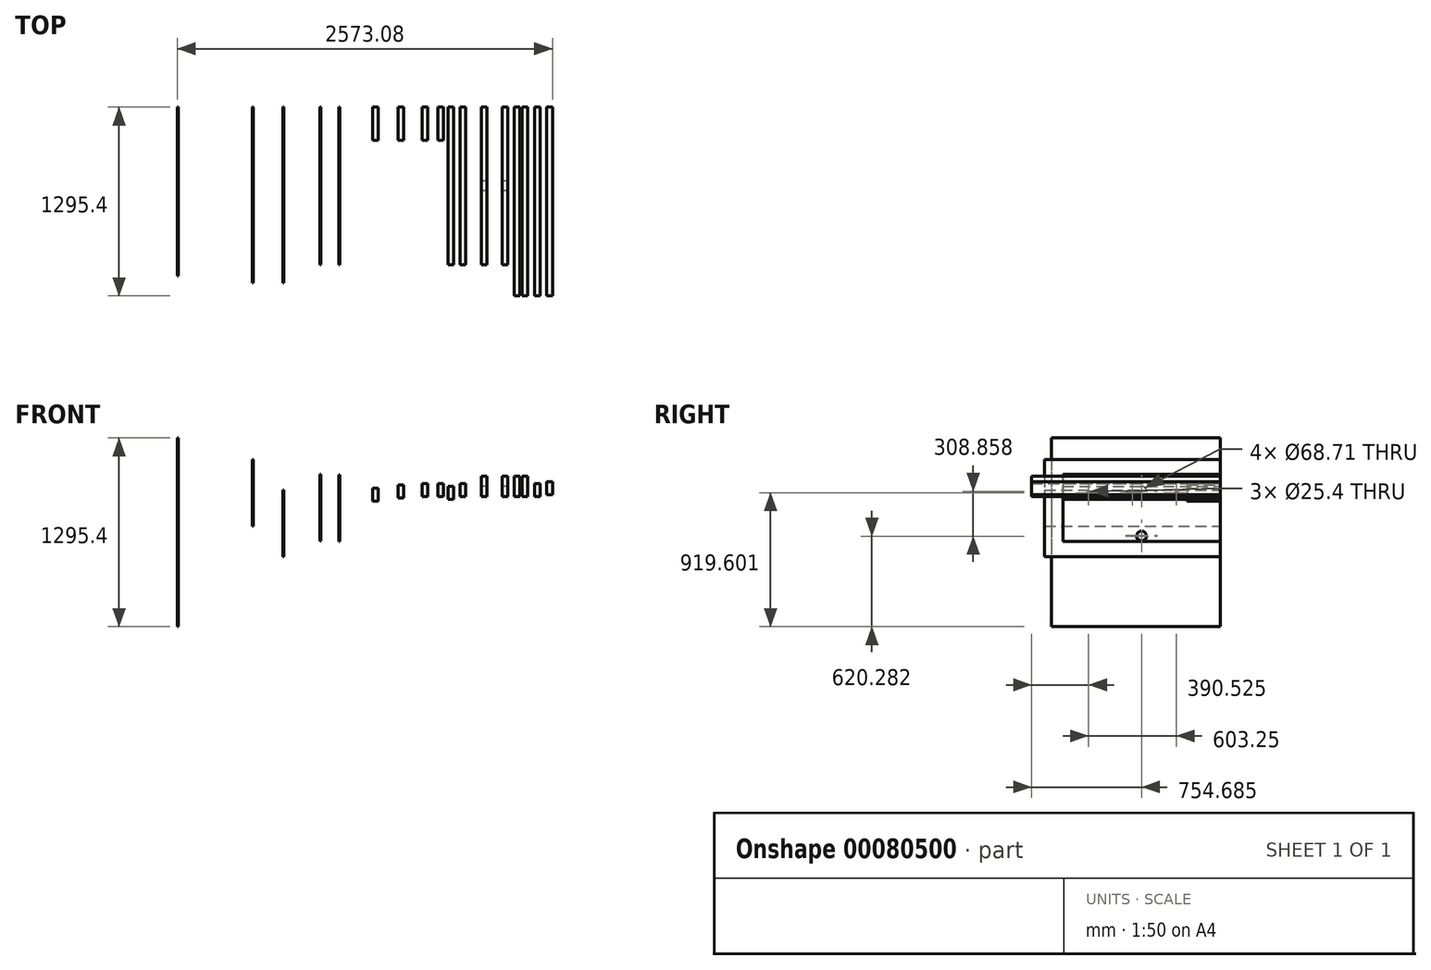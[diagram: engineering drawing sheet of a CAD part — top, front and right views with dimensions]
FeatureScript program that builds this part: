
annotation { "Feature Type Name" : "Feature", "Feature Type Description" : "" }
export const myFeature = defineFeature(function(context is Context, id is Id, definition is map)
    precondition{}
    {
        {
            var Q0;
            Q0=qCreatedBy(makeId("Front.planeOp"),FACE);
            var sketch = newSketch(context, id + "F0", { "sketchPlane" : qUnion([Q0])});
            skLineSegment(sketch, "E0.bottom", {"start": v(0, 0) * mm, "end": v(38.1, 0) * mm});
            skLineSegment(sketch, "E0.top", {"start": v(0, 139.7) * mm, "end": v(38.1, 139.7) * mm});
            skLineSegment(sketch, "E0.left", {"start": v(0, 0) * mm, "end": v(0, 139.7) * mm});
            skLineSegment(sketch, "E0.right", {"start": v(38.1, 0) * mm, "end": v(38.1, 139.7) * mm});
            skSolve(sketch);
        }
        {
            var Q0;
            Q0 = qSketchRegion(id + "F0", true);
            extrude(context, id + "F1", {"entities" : qUnion([Q0]), "depth" : 1295.4 * mm});
        }
        {
            var Q0;
            Q0=qCreatedBy(makeId("Front.planeOp"),FACE);
            var sketch = newSketch(context, id + "F2", { "sketchPlane" : qUnion([Q0])});
            skLineSegment(sketch, "E1.bottom", {"start": v(-55.83, 0) * mm, "end": v(-17.73, 0) * mm});
            skLineSegment(sketch, "E1.top", {"start": v(-55.83, 139.7) * mm, "end": v(-17.73, 139.7) * mm});
            skLineSegment(sketch, "E1.left", {"start": v(-55.83, 0) * mm, "end": v(-55.83, 139.7) * mm});
            skLineSegment(sketch, "E1.right", {"start": v(-17.73, 0) * mm, "end": v(-17.73, 139.7) * mm});
            skSolve(sketch);
        }
        {
            var Q0;
            Q0 = qSketchRegion(id + "F2", true);
            extrude(context, id + "F3", {"entities" : qUnion([Q0]), "depth" : 1295.4 * mm});
        }
        {
            var Q0;
            Q0=qCreatedBy(makeId("Front.planeOp"),FACE);
            var sketch = newSketch(context, id + "F4", { "sketchPlane" : qUnion([Q0])});
            skLineSegment(sketch, "E2.bottom", {"start": v(-138.64, 0) * mm, "end": v(-100.54, 0) * mm});
            skLineSegment(sketch, "E2.top", {"start": v(-138.64, 139.7) * mm, "end": v(-100.54, 139.7) * mm});
            skLineSegment(sketch, "E2.left", {"start": v(-138.64, 0) * mm, "end": v(-138.64, 139.7) * mm});
            skLineSegment(sketch, "E2.right", {"start": v(-100.54, 0) * mm, "end": v(-100.54, 139.7) * mm});
            skSolve(sketch);
        }
        {
            var Q0;
            Q0 = qSketchRegion(id + "F4", true);
            extrude(context, id + "F5", {"entities" : qUnion([Q0]), "depth" : 1081.43 * mm});
        }
        {
            var Q0;
            Q0=qCreatedBy(makeId("Front.planeOp"),FACE);
            var sketch = newSketch(context, id + "F6", { "sketchPlane" : qUnion([Q0])});
            skLineSegment(sketch, "E3.bottom", {"start": v(-281.16, 0) * mm, "end": v(-243.06, 0) * mm});
            skLineSegment(sketch, "E3.top", {"start": v(-281.16, 139.7) * mm, "end": v(-243.06, 139.7) * mm});
            skLineSegment(sketch, "E3.left", {"start": v(-281.16, 0) * mm, "end": v(-281.16, 139.7) * mm});
            skLineSegment(sketch, "E3.right", {"start": v(-243.06, 0) * mm, "end": v(-243.06, 139.7) * mm});
            skSolve(sketch);
        }
        {
            var Q0;
            Q0 = qSketchRegion(id + "F6", true);
            extrude(context, id + "F7", {"entities" : qUnion([Q0]), "depth" : 1081.43 * mm});
        }
        {
            var Q0;
            Q0=qCreatedBy(makeId("Front.planeOp"),FACE);
            var sketch = newSketch(context, id + "F8", { "sketchPlane" : qUnion([Q0])});
            skLineSegment(sketch, "E4.bottom", {"start": v(-507.98, 70.18) * mm, "end": v(-469.88, 70.18) * mm});
            skLineSegment(sketch, "E4.top", {"start": v(-507.98, -18.72) * mm, "end": v(-469.88, -18.72) * mm});
            skLineSegment(sketch, "E4.left", {"start": v(-507.98, 70.18) * mm, "end": v(-507.98, -18.72) * mm});
            skLineSegment(sketch, "E4.right", {"start": v(-469.88, 70.18) * mm, "end": v(-469.88, -18.72) * mm});
            skSolve(sketch);
        }
        {
            var Q0;
            Q0 = qSketchRegion(id + "F8", true);
            extrude(context, id + "F9", {"entities" : qUnion([Q0]), "depth" : 1081.43 * mm});
        }
        {
            var Q0;
            Q0=qCreatedBy(makeId("Front.planeOp"),FACE);
            var sketch = newSketch(context, id + "F10", { "sketchPlane" : qUnion([Q0])});
            skLineSegment(sketch, "E5.bottom", {"start": v(-426.13, 1.44) * mm, "end": v(-388.03, 1.44) * mm});
            skLineSegment(sketch, "E5.top", {"start": v(-426.13, 90.34) * mm, "end": v(-388.03, 90.34) * mm});
            skLineSegment(sketch, "E5.left", {"start": v(-426.13, 1.44) * mm, "end": v(-426.13, 90.34) * mm});
            skLineSegment(sketch, "E5.right", {"start": v(-388.03, 1.44) * mm, "end": v(-388.03, 90.34) * mm});
            skSolve(sketch);
        }
        {
            var Q0;
            Q0 = qSketchRegion(id + "F10", true);
            extrude(context, id + "F11", {"entities" : qUnion([Q0]), "depth" : 1081.43 * mm});
        }
        {
            var Q0;
            Q0=qCreatedBy(makeId("Front.planeOp"),FACE);
            var sketch = newSketch(context, id + "F12", { "sketchPlane" : qUnion([Q0])});
            skLineSegment(sketch, "E6.bottom", {"start": v(86.38, 88.9) * mm, "end": v(124.48, 88.9) * mm});
            skLineSegment(sketch, "E6.top", {"start": v(86.38, 0) * mm, "end": v(124.48, 0) * mm});
            skLineSegment(sketch, "E6.left", {"start": v(86.38, 88.9) * mm, "end": v(86.38, 0) * mm});
            skLineSegment(sketch, "E6.right", {"start": v(124.48, 88.9) * mm, "end": v(124.48, 0) * mm});
            skSolve(sketch);
        }
        {
            var Q0;
            Q0 = qSketchRegion(id + "F12", true);
            extrude(context, id + "F13", {"entities" : qUnion([Q0]), "depth" : 1295.4 * mm});
        }
        {
            var Q0;
            Q0=qCreatedBy(makeId("Front.planeOp"),FACE);
            var sketch = newSketch(context, id + "F14", { "sketchPlane" : qUnion([Q0])});
            skLineSegment(sketch, "E7.bottom", {"start": v(169.11, 101.24) * mm, "end": v(207.21, 101.24) * mm});
            skLineSegment(sketch, "E7.top", {"start": v(169.11, 12.34) * mm, "end": v(207.21, 12.34) * mm});
            skLineSegment(sketch, "E7.left", {"start": v(169.11, 101.24) * mm, "end": v(169.11, 12.34) * mm});
            skLineSegment(sketch, "E7.right", {"start": v(207.21, 101.24) * mm, "end": v(207.21, 12.34) * mm});
            skSolve(sketch);
        }
        {
            var Q0;
            Q0 = qSketchRegion(id + "F14", true);
            extrude(context, id + "F15", {"entities" : qUnion([Q0]), "depth" : 1295.4 * mm});
        }
        {
            var Q0;
            Q0=qCreatedBy(makeId("Front.planeOp"),FACE);
            var sketch = newSketch(context, id + "F16", { "sketchPlane" : qUnion([Q0])});
            skLineSegment(sketch, "E8.bottom", {"start": v(-687.17, 0) * mm, "end": v(-649.07, 0) * mm});
            skLineSegment(sketch, "E8.top", {"start": v(-687.17, 88.9) * mm, "end": v(-649.07, 88.9) * mm});
            skLineSegment(sketch, "E8.left", {"start": v(-687.17, 0) * mm, "end": v(-687.17, 88.9) * mm});
            skLineSegment(sketch, "E8.right", {"start": v(-649.07, 0) * mm, "end": v(-649.07, 88.9) * mm});
            skSolve(sketch);
        }
        {
            var Q0;
            Q0 = qSketchRegion(id + "F16", true);
            extrude(context, id + "F17", {"entities" : qUnion([Q0]), "depth" : 228.6 * mm});
        }
        {
            var Q0;
            Q0=qCreatedBy(makeId("Front.planeOp"),FACE);
            var sketch = newSketch(context, id + "F18", { "sketchPlane" : qUnion([Q0])});
            skLineSegment(sketch, "E9.bottom", {"start": v(-579.7, 88.9) * mm, "end": v(-541.6, 88.9) * mm});
            skLineSegment(sketch, "E9.top", {"start": v(-579.7, 0) * mm, "end": v(-541.6, 0) * mm});
            skLineSegment(sketch, "E9.left", {"start": v(-579.7, 88.9) * mm, "end": v(-579.7, 0) * mm});
            skLineSegment(sketch, "E9.right", {"start": v(-541.6, 88.9) * mm, "end": v(-541.6, 0) * mm});
            skSolve(sketch);
        }
        {
            var Q0;
            Q0 = qSketchRegion(id + "F18", true);
            extrude(context, id + "F19", {"entities" : qUnion([Q0]), "depth" : 228.6 * mm});
        }
        {
            var Q0;
            Q0=qCreatedBy(makeId("Front.planeOp"),FACE);
            var sketch = newSketch(context, id + "F20", { "sketchPlane" : qUnion([Q0])});
            skLineSegment(sketch, "E10.bottom", {"start": v(-1024.87, 57.76) * mm, "end": v(-986.77, 57.76) * mm});
            skLineSegment(sketch, "E10.top", {"start": v(-1024.87, -31.14) * mm, "end": v(-986.77, -31.14) * mm});
            skLineSegment(sketch, "E10.left", {"start": v(-1024.87, 57.76) * mm, "end": v(-1024.87, -31.14) * mm});
            skLineSegment(sketch, "E10.right", {"start": v(-986.77, 57.76) * mm, "end": v(-986.77, -31.14) * mm});
            skSolve(sketch);
        }
        {
            var Q0;
            Q0 = qSketchRegion(id + "F20", true);
            extrude(context, id + "F21", {"entities" : qUnion([Q0]), "depth" : 228.6 * mm});
        }
        {
            var Q0;
            Q0=qCreatedBy(makeId("Front.planeOp"),FACE);
            var sketch = newSketch(context, id + "F22", { "sketchPlane" : qUnion([Q0])});
            skLineSegment(sketch, "E11.bottom", {"start": v(-850.48, 79.15) * mm, "end": v(-812.38, 79.15) * mm});
            skLineSegment(sketch, "E11.top", {"start": v(-850.48, -9.75) * mm, "end": v(-812.38, -9.75) * mm});
            skLineSegment(sketch, "E11.left", {"start": v(-850.48, 79.15) * mm, "end": v(-850.48, -9.75) * mm});
            skLineSegment(sketch, "E11.right", {"start": v(-812.38, 79.15) * mm, "end": v(-812.38, -9.75) * mm});
            skSolve(sketch);
        }
        {
            var Q0;
            Q0 = qSketchRegion(id + "F22", true);
            extrude(context, id + "F23", {"entities" : qUnion([Q0]), "depth" : 228.6 * mm});
        }
        {
            var Q0;
            Q0=qCreatedBy(makeId("Front.planeOp"),FACE);
            var sketch = newSketch(context, id + "F24", { "sketchPlane" : qUnion([Q0])});
            skLineSegment(sketch, "E12.bottom", {"start": v(-1257.95, 148.34) * mm, "end": v(-1251.6, 148.34) * mm});
            skLineSegment(sketch, "E12.top", {"start": v(-1257.95, -308.86) * mm, "end": v(-1251.6, -308.86) * mm});
            skLineSegment(sketch, "E12.left", {"start": v(-1257.95, 148.34) * mm, "end": v(-1257.95, -308.86) * mm});
            skLineSegment(sketch, "E12.right", {"start": v(-1251.6, 148.34) * mm, "end": v(-1251.6, -308.86) * mm});
            skSolve(sketch);
        }
        {
            var Q0;
            Q0 = qSketchRegion(id + "F24", true);
            extrude(context, id + "F25", {"entities" : qUnion([Q0]), "depth" : 1081.43 * mm});
        }
        {
            var Q0;
            Q0=qCreatedBy(makeId("Front.planeOp"),FACE);
            var sketch = newSketch(context, id + "F26", { "sketchPlane" : qUnion([Q0])});
            skLineSegment(sketch, "E13.bottom", {"start": v(-1386.82, 152.9) * mm, "end": v(-1380.47, 152.9) * mm});
            skLineSegment(sketch, "E13.top", {"start": v(-1386.82, -304.3) * mm, "end": v(-1380.47, -304.3) * mm});
            skLineSegment(sketch, "E13.left", {"start": v(-1386.82, 152.9) * mm, "end": v(-1386.82, -304.3) * mm});
            skLineSegment(sketch, "E13.right", {"start": v(-1380.47, 152.9) * mm, "end": v(-1380.47, -304.3) * mm});
            skSolve(sketch);
        }
        {
            var Q0;
            Q0 = qSketchRegion(id + "F26", true);
            extrude(context, id + "F27", {"entities" : qUnion([Q0]), "depth" : 1081.43 * mm});
        }
        {
            var Q0;
            Q0=qCreatedBy(makeId("Front.planeOp"),FACE);
            var sketch = newSketch(context, id + "F28", { "sketchPlane" : qUnion([Q0])});
            skLineSegment(sketch, "E14.bottom", {"start": v(-1642.23, 46.34) * mm, "end": v(-1635.88, 46.34) * mm});
            skLineSegment(sketch, "E14.top", {"start": v(-1642.23, -410.86) * mm, "end": v(-1635.88, -410.86) * mm});
            skLineSegment(sketch, "E14.left", {"start": v(-1642.23, 46.34) * mm, "end": v(-1642.23, -410.86) * mm});
            skLineSegment(sketch, "E14.right", {"start": v(-1635.88, 46.34) * mm, "end": v(-1635.88, -410.86) * mm});
            skSolve(sketch);
        }
        {
            var Q0;
            Q0 = qSketchRegion(id + "F28", true);
            extrude(context, id + "F29", {"entities" : qUnion([Q0]), "depth" : 1206.5 * mm});
        }
        {
            var Q0;
            Q0=qCreatedBy(makeId("Front.planeOp"),FACE);
            var sketch = newSketch(context, id + "F30", { "sketchPlane" : qUnion([Q0])});
            skLineSegment(sketch, "E15.bottom", {"start": v(-1853.4, 253.18) * mm, "end": v(-1847.06, 253.18) * mm});
            skLineSegment(sketch, "E15.top", {"start": v(-1853.4, -204.02) * mm, "end": v(-1847.06, -204.02) * mm});
            skLineSegment(sketch, "E15.left", {"start": v(-1853.4, 253.18) * mm, "end": v(-1853.4, -204.02) * mm});
            skLineSegment(sketch, "E15.right", {"start": v(-1847.06, 253.18) * mm, "end": v(-1847.06, -204.02) * mm});
            skSolve(sketch);
        }
        {
            var Q0;
            Q0 = qSketchRegion(id + "F30", true);
            extrude(context, id + "F31", {"entities" : qUnion([Q0]), "depth" : 1206.5 * mm});
        }
        {
            var Q0;
            Q0=qCreatedBy(makeId("Front.planeOp"),FACE);
            var sketch = newSketch(context, id + "F32", { "sketchPlane" : qUnion([Q0])});
            skLineSegment(sketch, "E16.bottom", {"start": v(-2365.87, 403.09) * mm, "end": v(-2359.52, 403.09) * mm});
            skLineSegment(sketch, "E16.top", {"start": v(-2365.87, -892.31) * mm, "end": v(-2359.52, -892.31) * mm});
            skLineSegment(sketch, "E16.left", {"start": v(-2365.87, 403.09) * mm, "end": v(-2365.87, -892.31) * mm});
            skLineSegment(sketch, "E16.right", {"start": v(-2359.52, 403.09) * mm, "end": v(-2359.52, -892.31) * mm});
            skSolve(sketch);
        }
        {
            var Q0;
            Q0 = qSketchRegion(id + "F32", true);
            extrude(context, id + "F33", {"entities" : qUnion([Q0]), "depth" : 1157.63 * mm});
        }
        {
            var Q0;
            Q0=makeQuery(id+"F7.opExtrude","SWEPT_FACE",FACE,{"disambiguationData":[OSD([sQuery(id+"F6.wireOp",EDGE,"E3.left")])]});
            var sketch = newSketch(context, id + "F34", { "sketchPlane" : qUnion([Q0])});
            skCircle(sketch, "E17", {"center": v(540.72, 36.83) * mm, "radius": 34.35 * mm});
            skSolve(sketch);
        }
        {
            var Q0;
            Q0 = qSketchRegion(id + "F34", true);
            extrude(context, id + "F35", {"entities" : qUnion([Q0]), "operationType" : NewBodyOperationType.REMOVE, "oppositeDirection" : true, "depth" : 38.1 * mm});
        }
        {
            var Q0;
            Q0=makeQuery(id+"F5.opExtrude","SWEPT_FACE",FACE,{"disambiguationData":[OSD([sQuery(id+"F4.wireOp",EDGE,"E2.left")])]});
            var sketch = newSketch(context, id + "F36", { "sketchPlane" : qUnion([Q0])});
            skCircle(sketch, "E18", {"center": v(540.72, 36.83) * mm, "radius": 34.35 * mm});
            skPoint(sketch, "E18.centerSnap0", {"position": v(540.72, 139.7) * mm});
            skSolve(sketch);
        }
        {
            var Q0;
            Q0 = qSketchRegion(id + "F36", true);
            extrude(context, id + "F37", {"entities" : qUnion([Q0]), "operationType" : NewBodyOperationType.REMOVE, "oppositeDirection" : true, "depth" : 38.1 * mm});
        }
        {
            var Q0;
            Q0=makeQuery(id+"F25.opExtrude","SWEPT_FACE",FACE,{"disambiguationData":[OSD([sQuery(id+"F24.wireOp",EDGE,"E12.left")])]});
            var sketch = newSketch(context, id + "F38", { "sketchPlane" : qUnion([Q0])});
            skCircle(sketch, "E19", {"center": v(540.72, -272.03) * mm, "radius": 34.35 * mm});
            skSolve(sketch);
        }
        {
            var Q0;
            Q0 = qSketchRegion(id + "F38", true);
            extrude(context, id + "F39", {"entities" : qUnion([Q0]), "operationType" : NewBodyOperationType.REMOVE, "oppositeDirection" : true, "depth" : 25.4 * mm});
        }
        {
            var Q0;
            Q0=makeQuery(id+"F27.opExtrude","SWEPT_FACE",FACE,{"disambiguationData":[OSD([sQuery(id+"F26.wireOp",EDGE,"E13.left")])]});
            var sketch = newSketch(context, id + "F40", { "sketchPlane" : qUnion([Q0])});
            skCircle(sketch, "E20", {"center": v(540.72, -267.47) * mm, "radius": 34.35 * mm});
            skSolve(sketch);
        }
        {
            var Q0;
            Q0 = qSketchRegion(id + "F40", true);
            extrude(context, id + "F41", {"entities" : qUnion([Q0]), "operationType" : NewBodyOperationType.REMOVE, "oppositeDirection" : true, "depth" : 25.4 * mm});
        }
        {
            var Q0;
            Q0=makeQuery(id+"F29.opExtrude","SWEPT_FACE",FACE,{"disambiguationData":[OSD([sQuery(id+"F28.wireOp",EDGE,"E14.left")])]});
            var sketch = newSketch(context, id + "F42", { "sketchPlane" : qUnion([Q0])});
            skCircle(sketch, "E21", {"center": v(301.63, 27.3) * mm, "radius": 12.7 * mm});
            skCircle(sketch, "E22", {"center": v(603.25, 27.3) * mm, "radius": 12.7 * mm});
            skCircle(sketch, "E23", {"center": v(904.88, 27.3) * mm, "radius": 12.7 * mm});
            skSolve(sketch);
        }
        {
            var Q0;
            Q0 = qSketchRegion(id + "F42", true);
            extrude(context, id + "F43", {"entities" : qUnion([Q0]), "operationType" : NewBodyOperationType.REMOVE, "oppositeDirection" : true, "depth" : 25.4 * mm});
        }
    });
